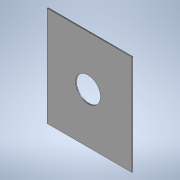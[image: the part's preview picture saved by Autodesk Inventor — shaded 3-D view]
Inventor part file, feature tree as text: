
AUTODESK INVENTOR PART (.ipt)
format: ipt  version: 2021 (Build 250183000, 183)  size: 103,936 bytes
history: native  units: in
note: dims shown in document units (in); Inventor stores cm internally (conversion verified against a paired STEP export)
features: extrude x2, sketch x2
ambient origin geometry x8: Origin, YZ Plane, XZ Plane, XY Plane, X Axis, Y Axis, Z Axis, Center Point
bodies: Solid1 (feature_tree)
feature tree (4):
  extrude  "Extrusion1"  Depth=0.0669in
  extrude  "Extrusion2"  TaperAngle=0.0deg  [1 undecoded]
  sketch  "Sketch1"  dims[d0=0.0787in d1=0.0669in]
  sketch  "Sketch2"  dims[d2=0.0008in d3=0.0in d5=0.0in d6=0.0in d9=0.0197in d10=0.0646in d11=0.0787in]
note: 1 required parameter value undecoded (feature->parameter linkage not recoverable at this tier; creation-order binding heuristic only, values carry confidence <= 0.55)
